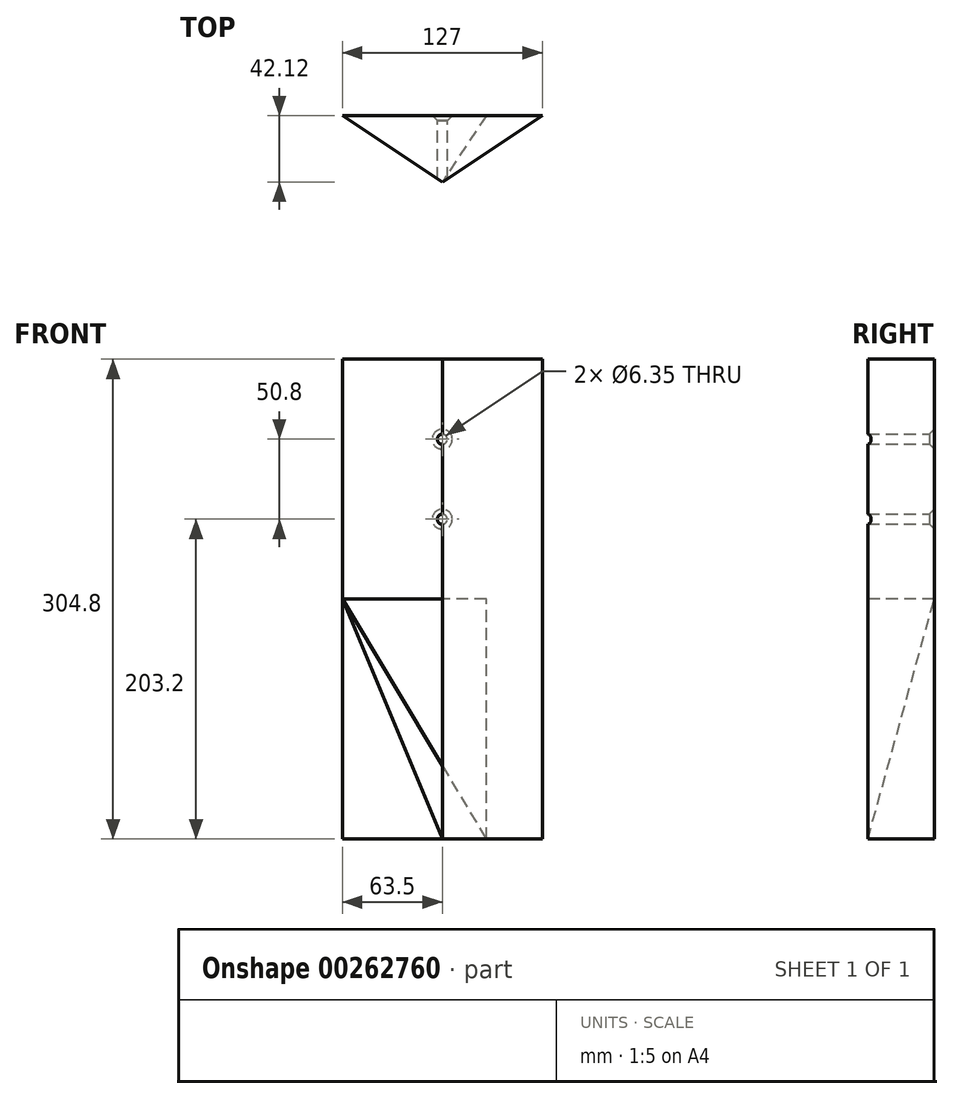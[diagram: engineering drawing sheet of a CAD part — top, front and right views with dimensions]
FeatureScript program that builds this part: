
annotation { "Feature Type Name" : "Feature", "Feature Type Description" : "" }
export const myFeature = defineFeature(function(context is Context, id is Id, definition is map)
    precondition{}
    {
        {
            var Q0;
            Q0=qCreatedBy(makeId("Top.planeOp"),FACE);
            var sketch = newSketch(context, id + "F0", { "sketchPlane" : qUnion([Q0])});
            skLineSegment(sketch, "E0", {"start": v(-63.5, 0) * mm, "end": v(63.5, 0) * mm});
            skLineSegment(sketch, "E1", {"start": v(-63.5, 0) * mm, "end": v(0, -42.12) * mm});
            skLineSegment(sketch, "E2", {"start": v(0, -42.12) * mm, "end": v(63.5, 0) * mm});
            skSolve(sketch);
        }
        {
            var Q0;
            Q0=makeQuery(id+"F0.imprint","IMPRINT",FACE,{"disambiguationData":[TD([[makeQuery(id+"F0.imprint","IMPRINT",EDGE,{"derivedFrom":sQuery(id+"F0.wireOp",EDGE,"E0")}),-1.0]])]});
            extrude(context, id + "F1", {"entities" : qUnion([Q0]), "depth" : 304.8 * mm});
        }
        {
            var Q0;
            Q0=makeQuery(id+"F1.opExtrude","SWEPT_FACE",FACE,{"disambiguationData":[OSD([sQuery(id+"F0.wireOp",EDGE,"E1")])]});
            var sketch = newSketch(context, id + "F2", { "sketchPlane" : qUnion([Q0])});
            skLineSegment(sketch, "E3", {"start": v(23.28, 0) * mm, "end": v(-52.92, 152.4) * mm});
            skLineSegment(sketch, "E4", {"start": v(-52.92, 152.4) * mm, "end": v(23.28, 152.4) * mm});
            skSolve(sketch);
        }
        {
            var Q0;
            {var subQ0=sQuery(id+"F2.wireOp",EDGE,"E3");Q0=makeQuery(id+"F2.imprint","IMPRINT",FACE,{"disambiguationData":[TD([[makeQuery(id+"F2.imprint","IMPRINT",EDGE,{"derivedFrom":subQ0}),-1.0]])]});}
            extrude(context, id + "F3", {"entities" : qUnion([Q0]), "operationType" : NewBodyOperationType.REMOVE, "oppositeDirection" : true, "depth" : 50.8 * mm});
        }
        {
            var Q0;
            {var subQ0=sQuery(id+"F0.wireOp",EDGE,"E2");var subQ2=sQuery(id+"F0.wireOp",EDGE,"E0");Q0=makeQuery(id+"F3.boolean.opBoolean","SPLIT",FACE,{"disambiguationData":[TD([makeQuery(id+"F1.opExtrude","SWEPT_FACE",FACE,{"disambiguationData":[OSD([subQ0])]})])],"derivedFrom":makeQuery(id+"F1.opExtrude","SWEPT_FACE",FACE,{"disambiguationData":[OSD([subQ2])]})});}
            var sketch = newSketch(context, id + "F4", { "sketchPlane" : qUnion([Q0])});
            skLineSegment(sketch, "E5", {"start": v(0, 304.8) * mm, "end": v(0, 152.4) * mm});
            skCircle(sketch, "E6", {"center": v(0, 254) * mm, "radius": 6.35 * mm});
            skCircle(sketch, "E7", {"center": v(0, 203.2) * mm, "radius": 6.35 * mm});
            skSolve(sketch);
        }
        {
            var Q0;
            Q0=sQuery(id+"F4.wireOp",VERTEX,"E7.center");
            var Q1;
            Q1=sQuery(id+"F4.wireOp",VERTEX,"E6.center");
            var Q2;
            Q2=makeQuery(id+"F3.boolean.opBoolean","SPLIT",BODY,{"disambiguationData":[OD(0.0)],"derivedFrom":makeQuery(id+"F1.opExtrude","SWEPT_BODY",BODY,{"disambiguationData":[OSD([sQuery(id+"F0.wireOp",EDGE,"E0"),sQuery(id+"F0.wireOp",EDGE,"E1"),sQuery(id+"F0.wireOp",EDGE,"E2")])]})});
            hole(context, id + "F5", {"style" : HoleStyle.C_SINK, "endStyle" : HoleEndStyle.THROUGH, "holeDiameter" : 6.35 * mm, "cSinkDiameter" : 12.7 * mm, "cSinkAngle" : 90 * degree, "tappedDepth" : 12.7 * mm, "tapClearance" : 3, "locations" : qUnion([Q0, Q1]), "scope" : qUnion([Q2])});
        }
    });
